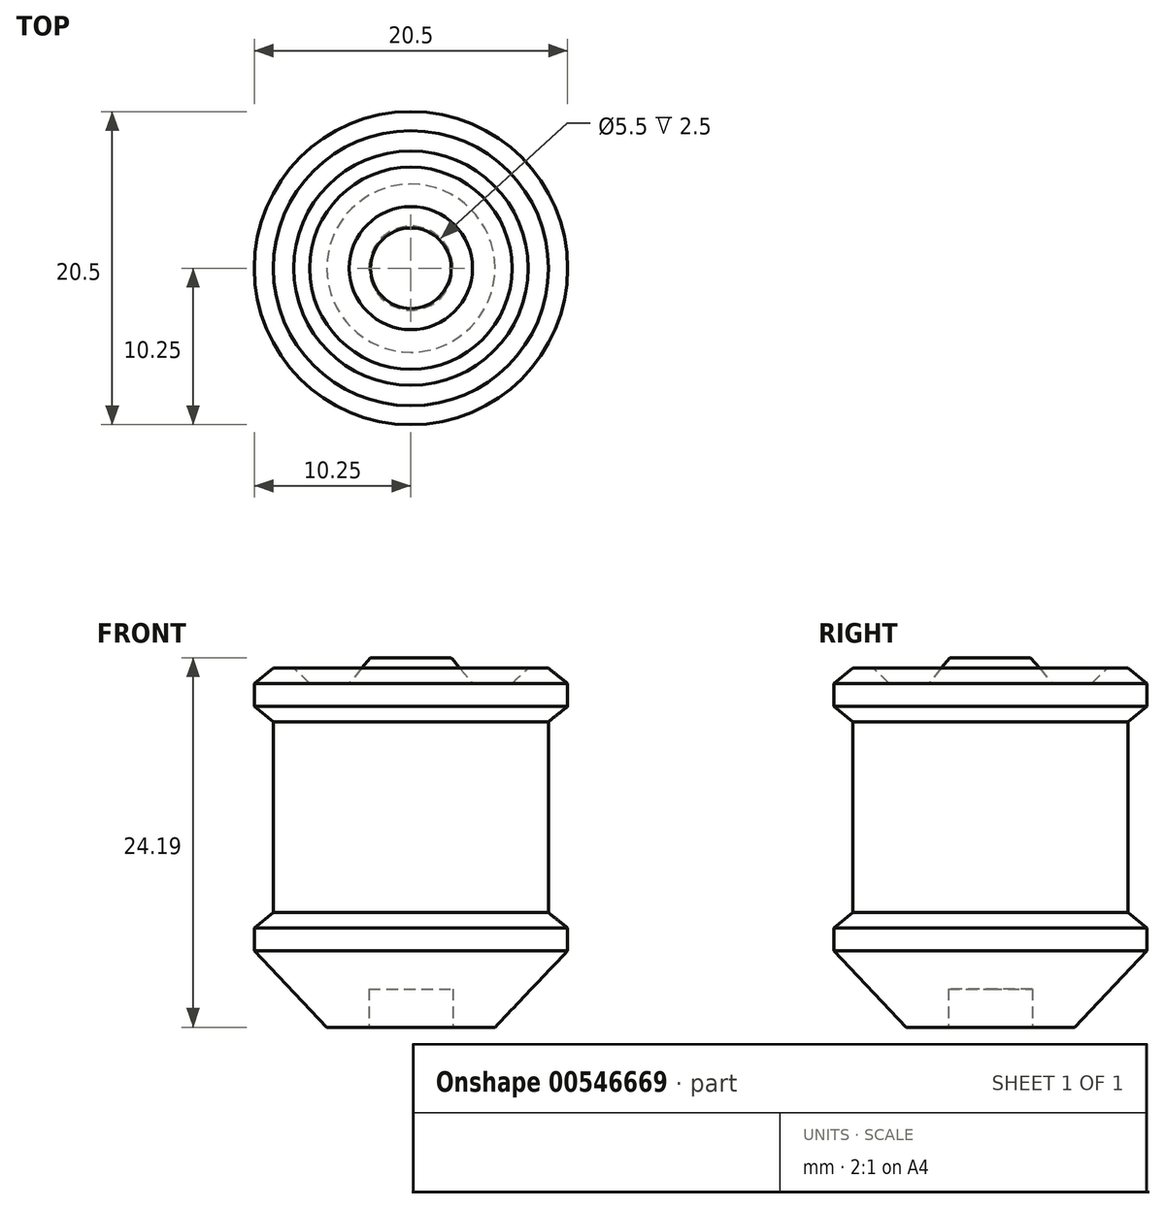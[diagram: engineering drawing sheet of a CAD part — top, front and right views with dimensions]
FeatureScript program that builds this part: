
annotation { "Feature Type Name" : "Feature", "Feature Type Description" : "" }
export const myFeature = defineFeature(function(context is Context, id is Id, definition is map)
    precondition{}
    {
        {
            var Q0;
            Q0=qCreatedBy(makeId("Front.planeOp"),FACE);
            var sketch = newSketch(context, id + "F0", { "sketchPlane" : qUnion([Q0])});
            skLineSegment(sketch, "E0", {"start": v(0, 0) * mm, "end": v(5.5, 0) * mm});
            skLineSegment(sketch, "E1", {"start": v(0, 23.5) * mm, "end": v(0, 0) * mm});
            skLineSegment(sketch, "E2", {"start": v(9, 23.5) * mm, "end": v(10.25, 22.5) * mm});
            skLineSegment(sketch, "E3", {"start": v(10.25, 21) * mm, "end": v(9, 20) * mm});
            skLineSegment(sketch, "E4", {"start": v(9, 7.5) * mm, "end": v(10.25, 6.5) * mm});
            skLineSegment(sketch, "E5", {"start": v(10.25, 5) * mm, "end": v(5.5, 0) * mm});
            skLineSegment(sketch, "E6", {"start": v(9, 20) * mm, "end": v(9, 7.5) * mm});
            skLineSegment(sketch, "E7", {"start": v(10.25, 22.5) * mm, "end": v(10.25, 21) * mm});
            skLineSegment(sketch, "E8", {"start": v(10.25, 6.5) * mm, "end": v(10.25, 5) * mm});
            skLineSegment(sketch, "E9", {"start": v(4.03, 22.51) * mm, "end": v(6.62, 22.51) * mm});
            skLineSegment(sketch, "E10.trimOffspring", {"start": v(7.67, 23.5) * mm, "end": v(9, 23.5) * mm});
            skLineSegment(sketch, "E11", {"start": v(4.03, 22.51) * mm, "end": v(2.64, 24.2) * mm});
            skLineSegment(sketch, "E12", {"start": v(2.64, 24.2) * mm, "end": v(0, 24.2) * mm});
            skLineSegment(sketch, "E13", {"start": v(0, 24.2) * mm, "end": v(0, 23.5) * mm});
            skLineSegment(sketch, "E14", {"start": v(7.67, 23.5) * mm, "end": v(6.62, 22.51) * mm});
            skSolve(sketch);
        }
        {
            var Q0;
            Q0=qSketchRegion(id+"F0",true);
            var Q1;
            Q1=sQuery(id+"F0.wireOp",EDGE,"E1");
            revolve(context, id + "F1", {"entities" : qUnion([Q0]), "axis" : qUnion([Q1]), "revolveType" : RevolveType.FULL});
        }
        {
            var Q0;
            Q0=makeQuery(id+"F1.opRevolve","SWEPT_FACE",FACE,{"disambiguationData":[OSD([sQuery(id+"F0.wireOp",EDGE,"E0")])]});
            var sketch = newSketch(context, id + "F2", { "sketchPlane" : qUnion([Q0])});
            skCircle(sketch, "E15", {"center": v(0, 0) * mm, "radius": 2.75 * mm});
            skSolve(sketch);
        }
        {
            var Q0;
            Q0=qSketchRegion(id+"F2",true);
            extrude(context, id + "F3", {"entities" : qUnion([Q0]), "operationType" : NewBodyOperationType.REMOVE, "oppositeDirection" : true, "depth" : 2.5 * mm});
        }
    });
